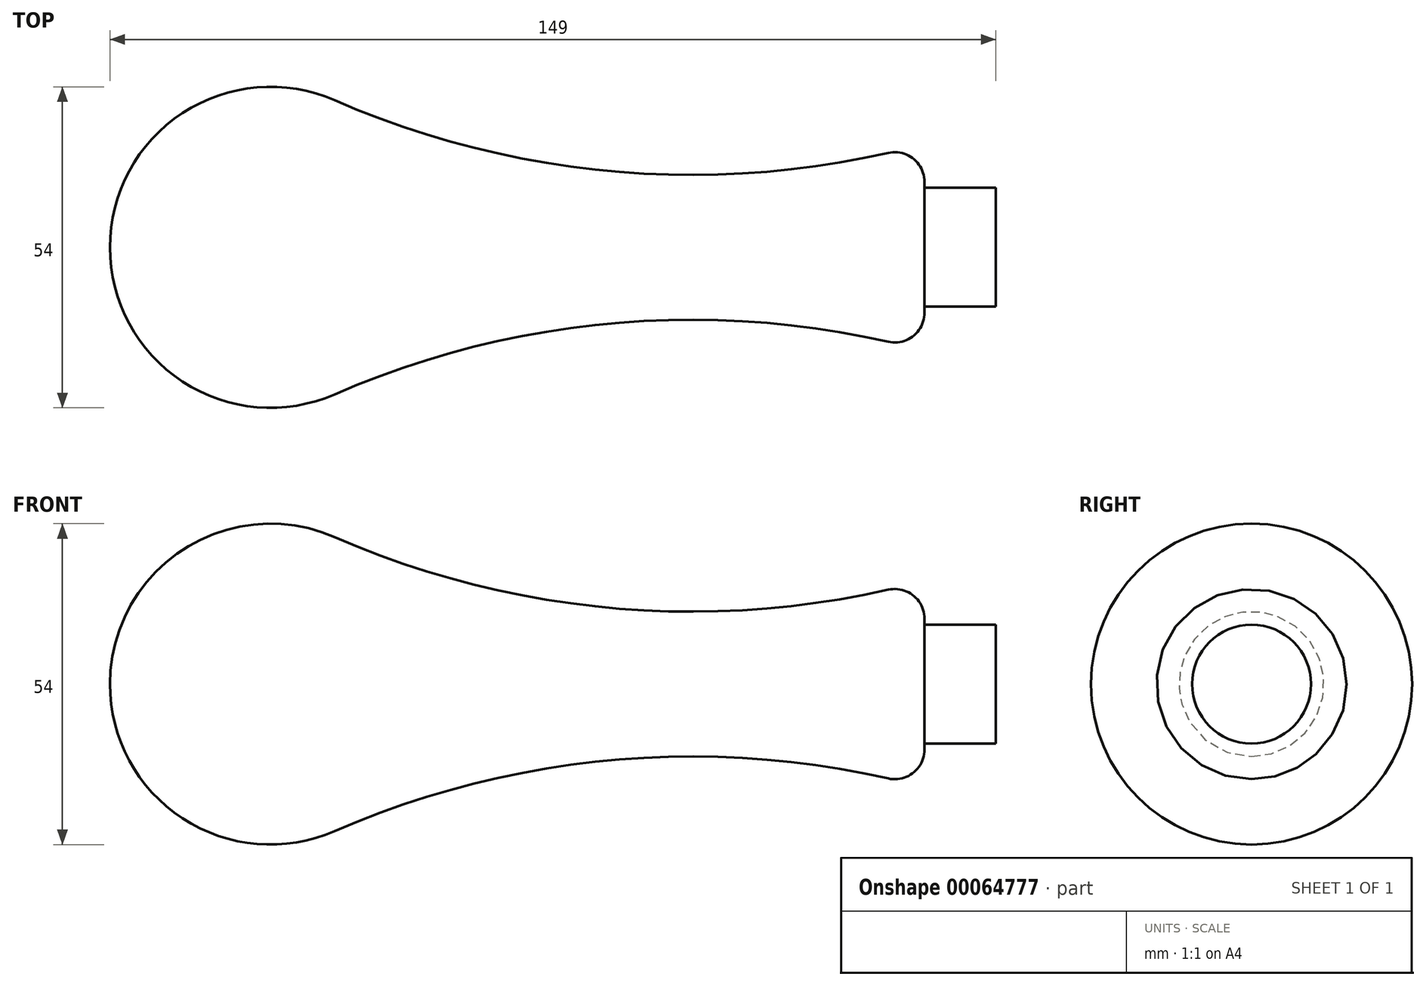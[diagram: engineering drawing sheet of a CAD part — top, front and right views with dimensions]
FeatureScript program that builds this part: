
annotation { "Feature Type Name" : "Feature", "Feature Type Description" : "" }
export const myFeature = defineFeature(function(context is Context, id is Id, definition is map)
    precondition{}
    {
        {
            var Q0;
            Q0=qCreatedBy(makeId("Front.planeOp"),FACE);
            var sketch = newSketch(context, id + "F0", { "sketchPlane" : qUnion([Q0])});
            skArc(sketch, "E0", {"start": v(10.8, 24.74) * mm, "mid": v(-14.78, 22.6) * mm, "end": v(-27, 0) * mm});
            skLineSegment(sketch, "E1", {"start": v(0, 0) * mm, "end": v(122, 0) * mm});
            skLineSegment(sketch, "E2", {"start": v(0, 0) * mm, "end": v(-27, 0) * mm, "construction": true});
            skLineSegment(sketch, "E3", {"start": v(122, 0) * mm, "end": v(122, 10) * mm});
            skLineSegment(sketch, "E4", {"start": v(122, 10) * mm, "end": v(110, 10) * mm});
            skLineSegment(sketch, "E5", {"start": v(110, 10) * mm, "end": v(110, 11) * mm});
            skArc(sketch, "E6", {"start": v(110, 11) * mm, "mid": v(108.12, 14.9) * mm, "end": v(103.9, 15.88) * mm});
            skArc(sketch, "E7", {"start": v(10.8, 24.74) * mm, "mid": v(56.65, 12.87) * mm, "end": v(103.9, 15.88) * mm});
            skSolve(sketch);
        }
        {
            var Q0;
            Q0=sQuery(id+"F0.wireOp",EDGE,"E0");
            var Q1;
            Q1=sQuery(id+"F0.wireOp",EDGE,"E7");
            var Q2;
            Q2=sQuery(id+"F0.wireOp",EDGE,"E6");
            var Q3;
            Q3=sQuery(id+"F0.wireOp",EDGE,"E4");
            var Q4;
            Q4=sQuery(id+"F0.wireOp",EDGE,"E3");
            var Q5;
            Q5=sQuery(id+"F0.wireOp",EDGE,"E5");
            var Q6;
            Q6=sQuery(id+"F0.wireOp",EDGE,"E1");
            revolve(context, id + "F1", {"bodyType" : ToolBodyType.SURFACE, "surfaceEntities" : qUnion([Q0, Q1, Q2, Q3, Q4, Q5]), "axis" : qUnion([Q6]), "revolveType" : RevolveType.FULL});
        }
    });
